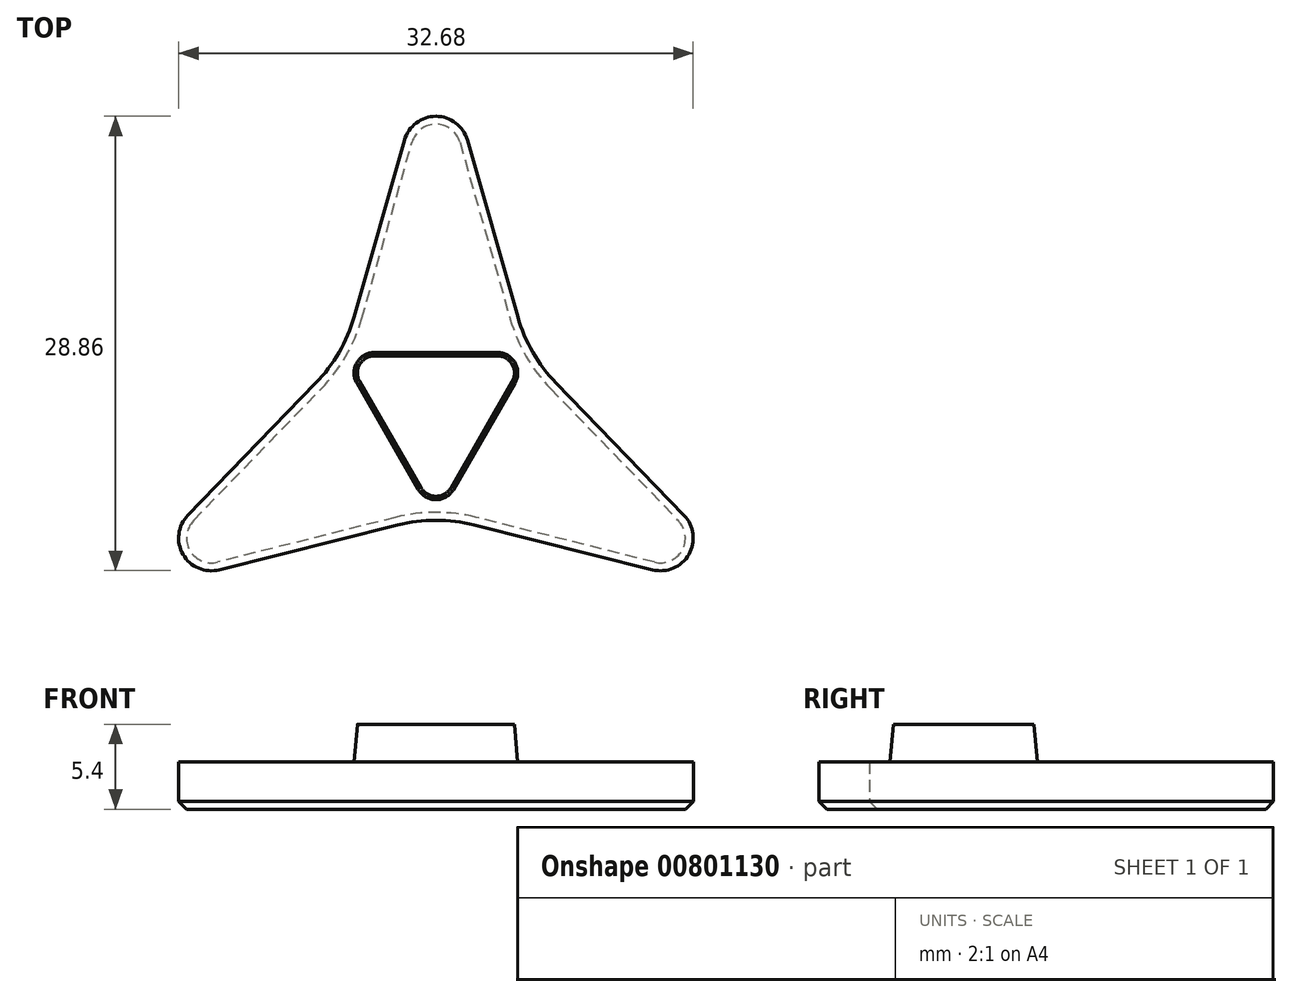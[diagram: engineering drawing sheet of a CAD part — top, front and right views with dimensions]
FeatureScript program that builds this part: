
annotation { "Feature Type Name" : "Feature", "Feature Type Description" : "" }
export const myFeature = defineFeature(function(context is Context, id is Id, definition is map)
    precondition{}
    {
        {
            var Q0;
            Q0=qCreatedBy(makeId("Top.planeOp"),FACE);
            var sketch = newSketch(context, id + "F0", { "sketchPlane" : qUnion([Q0])});
            skCircle(sketch, "E0.cCircle", {"center": v(0, 0) * mm, "radius": 3.55 * mm, "construction": true});
            skLineSegment(sketch, "E0.0", {"start": v(-3.9, 3.55) * mm, "end": v(3.9, 3.55) * mm});
            skLineSegment(sketch, "E0.1", {"start": v(5.02, 1.6) * mm, "end": v(1.13, -5.15) * mm});
            skLineSegment(sketch, "E0.2", {"start": v(-1.13, -5.15) * mm, "end": v(-5.02, 1.6) * mm});
            skPoint(sketch, "E0.0.midPoint", {"position": v(0, 3.55) * mm});
            skPoint(sketch, "E1.visualSharp", {"position": v(0, -7.1) * mm});
            skArc(sketch, "E1.filletArc", {"start": v(-1.13, -5.15) * mm, "mid": v(0, -5.8) * mm, "end": v(1.13, -5.15) * mm});
            skPoint(sketch, "E2.visualSharp", {"position": v(-6.15, 3.55) * mm});
            skArc(sketch, "E2.filletArc", {"start": v(-3.9, 3.55) * mm, "mid": v(-5.02, 2.9) * mm, "end": v(-5.02, 1.6) * mm});
            skPoint(sketch, "E3.visualSharp", {"position": v(6.15, 3.55) * mm});
            skArc(sketch, "E3.filletArc", {"start": v(5.02, 1.6) * mm, "mid": v(5.02, 2.9) * mm, "end": v(3.9, 3.55) * mm});
            skSolve(sketch);
        }
        {
            var Q0;
            Q0=makeQuery(id+"F0.imprint","IMPRINT",FACE,{"disambiguationData":[TD([[makeQuery(id+"F0.imprint","IMPRINT",EDGE,{"derivedFrom":sQuery(id+"F0.wireOp",EDGE,"E0.0")}),-1.0]])]});
            extrude(context, id + "F1", {"entities" : qUnion([Q0]), "depth" : 2.4 * mm, "offsetDistance" : 25 * mm, "hasDraft" : true, "draftAngle" : 5 * degree, "draftPullDirection" : true});
        }
        {
            var Q0;
            Q0=makeQuery(id+"F1.opExtrude","CAP_FACE",FACE,{"disambiguationData":[OSD([sQuery(id+"F0.wireOp",EDGE,"E0.0"),sQuery(id+"F0.wireOp",EDGE,"E0.1"),sQuery(id+"F0.wireOp",EDGE,"E0.2"),sQuery(id+"F0.wireOp",EDGE,"E1.filletArc"),sQuery(id+"F0.wireOp",EDGE,"E2.filletArc"),sQuery(id+"F0.wireOp",EDGE,"E3.filletArc")])],"isStart":true});
            var sketch = newSketch(context, id + "F2", { "sketchPlane" : qUnion([Q0])});
            skLineSegment(sketch, "E4", {"start": v(0, 0) * mm, "end": v(-7.58, -4.38) * mm, "construction": true});
            skLineSegment(sketch, "E5", {"start": v(-5.89, -3.4) * mm, "end": v(-2, -17.04) * mm});
            skLineSegment(sketch, "E6", {"start": v(0, 0) * mm, "end": v(7.45, -4.3) * mm, "construction": true});
            skLineSegment(sketch, "E7", {"start": v(2, -17.04) * mm, "end": v(5.89, -3.4) * mm});
            skPoint(sketch, "E8.visualSharp", {"position": v(0, -24.06) * mm});
            skArc(sketch, "E8.filletArc", {"start": v(-2, -17.04) * mm, "mid": v(0, -18.55) * mm, "end": v(2, -17.04) * mm});
            skLineSegment(sketch, "E9.1.0", {"start": v(5.89, -3.4) * mm, "end": v(15.76, 6.79) * mm});
            skArc(sketch, "E9.1.1", {"start": v(15.76, 6.79) * mm, "mid": v(16.06, 9.27) * mm, "end": v(13.76, 10.25) * mm});
            skLineSegment(sketch, "E9.1.2", {"start": v(13.76, 10.25) * mm, "end": v(0, 6.8) * mm});
            skLineSegment(sketch, "E9.2.0", {"start": v(0, 6.8) * mm, "end": v(-13.76, 10.25) * mm});
            skArc(sketch, "E9.2.1", {"start": v(-13.76, 10.25) * mm, "mid": v(-16.06, 9.27) * mm, "end": v(-15.76, 6.79) * mm});
            skLineSegment(sketch, "E9.2.2", {"start": v(-15.76, 6.79) * mm, "end": v(-5.89, -3.4) * mm});
            skPoint(sketch, "E9.center", {"position": v(0, 0) * mm});
            skSolve(sketch);
        }
        {
            var Q0;
            Q0=qSketchRegion(id+"F2",true);
            extrude(context, id + "F3", {"entities" : qUnion([Q0]), "operationType" : NewBodyOperationType.ADD, "depth" : 3 * mm, "offsetDistance" : 25 * mm});
        }
        {
            var Q0;
            Q0=makeQuery(id+"F3.opExtrude","SWEPT_EDGE",EDGE,{"disambiguationData":[OSD([sQuery(id+"F2.wireOp",EDGE,"E9.1.2"),sQuery(id+"F2.wireOp",EDGE,"E9.2.0")])]});
            var Q1;
            Q1=makeQuery(id+"F3.opExtrude","SWEPT_EDGE",EDGE,{"disambiguationData":[OSD([sQuery(id+"F2.wireOp",EDGE,"E7"),sQuery(id+"F2.wireOp",EDGE,"E9.1.0")])]});
            var Q2;
            Q2=makeQuery(id+"F3.opExtrude","SWEPT_EDGE",EDGE,{"disambiguationData":[OSD([sQuery(id+"F2.wireOp",EDGE,"E5"),sQuery(id+"F2.wireOp",EDGE,"E9.2.2")])]});
            fillet(context, id + "F4", {"entities" : qUnion([Q0, Q1, Q2]), "radius" : 10 * mm, "tangentPropagation" : true, "allowEdgeOverflow" : false});
        }
        {
            var Q0;
            Q0=makeQuery(id+"F3.opExtrude","CAP_FACE",FACE,{"disambiguationData":[OSD([sQuery(id+"F2.wireOp",EDGE,"E5"),sQuery(id+"F2.wireOp",EDGE,"E7"),sQuery(id+"F2.wireOp",EDGE,"E8.filletArc"),sQuery(id+"F2.wireOp",EDGE,"E9.1.0"),sQuery(id+"F2.wireOp",EDGE,"E9.1.1"),sQuery(id+"F2.wireOp",EDGE,"E9.1.2"),sQuery(id+"F2.wireOp",EDGE,"E9.2.0"),sQuery(id+"F2.wireOp",EDGE,"E9.2.1"),sQuery(id+"F2.wireOp",EDGE,"E9.2.2")])],"isStart":false});
            chamfer(context, id + "F5", {"entities" : qUnion([Q0]), "width" : 0.5 * mm, "tangentPropagation" : true});
        }
    });
